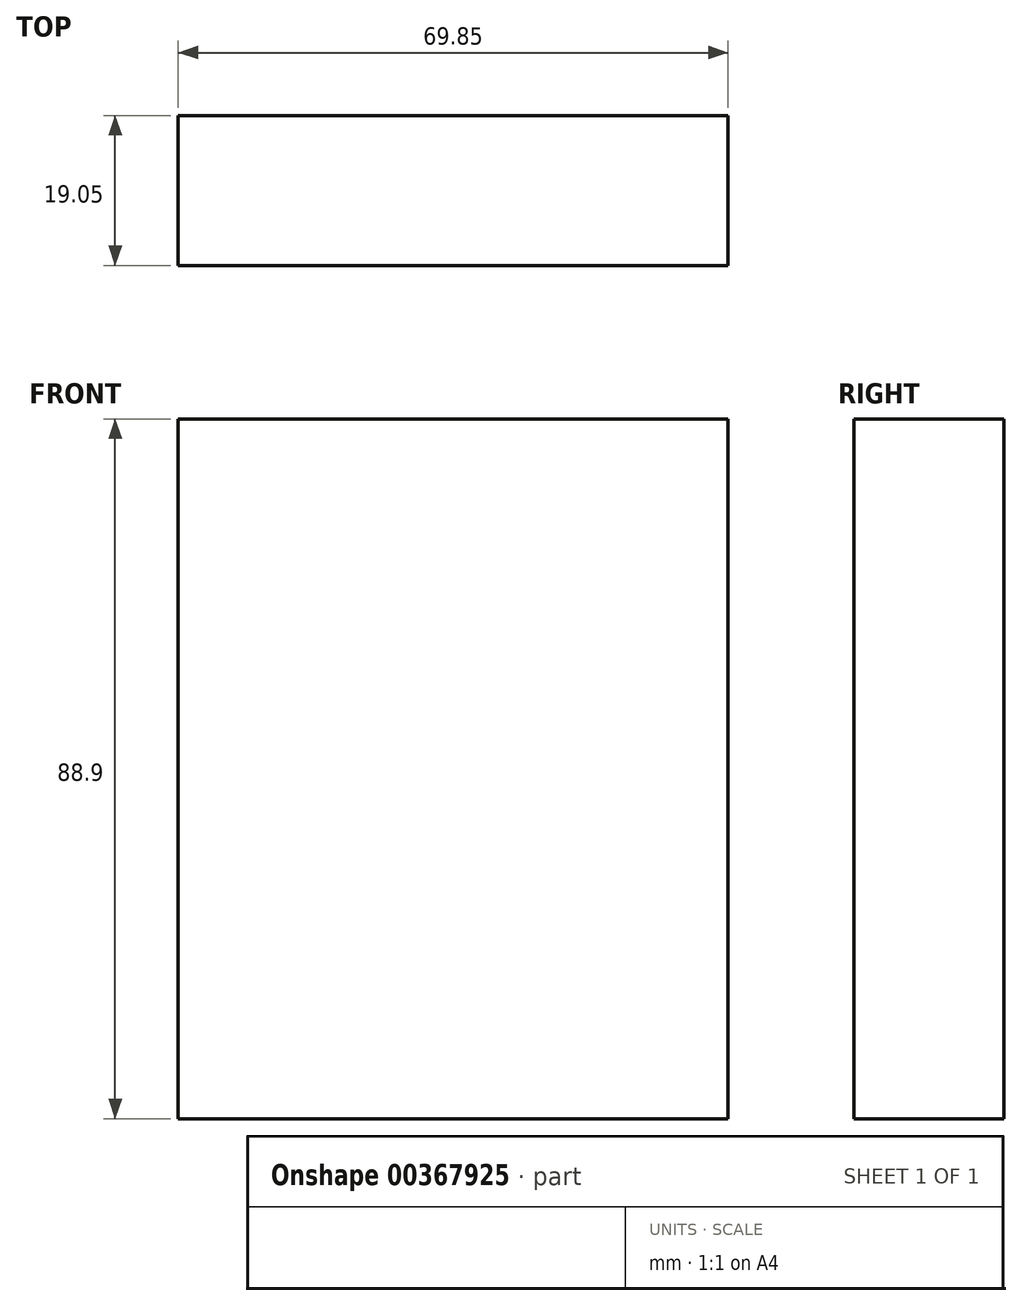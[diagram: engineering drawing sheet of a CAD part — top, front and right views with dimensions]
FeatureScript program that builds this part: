
annotation { "Feature Type Name" : "Feature", "Feature Type Description" : "" }
export const myFeature = defineFeature(function(context is Context, id is Id, definition is map)
    precondition{}
    {
        {
            var Q0;
            Q0=qCreatedBy(makeId("Front.planeOp"),FACE);
            var sketch = newSketch(context, id + "F0", { "sketchPlane" : qUnion([Q0])});
            skLineSegment(sketch, "E0.bottom", {"start": v(-88.51, 77.44) * mm, "end": v(-18.66, 77.44) * mm});
            skLineSegment(sketch, "E0.top", {"start": v(-88.51, -11.46) * mm, "end": v(-18.66, -11.46) * mm});
            skLineSegment(sketch, "E0.left", {"start": v(-88.51, 77.44) * mm, "end": v(-88.51, -11.46) * mm});
            skLineSegment(sketch, "E0.right", {"start": v(-18.66, 77.44) * mm, "end": v(-18.66, -11.46) * mm});
            skSolve(sketch);
        }
        {
            var Q0;
            Q0=makeQuery(id+"F0.imprint","IMPRINT",FACE,{"disambiguationData":[TD([[makeQuery(id+"F0.imprint","IMPRINT",EDGE,{"derivedFrom":sQuery(id+"F0.wireOp",EDGE,"E0.bottom")}),-1.0]])]});
            extrude(context, id + "F1", {"entities" : qUnion([Q0]), "depth" : 19.05 * mm});
        }
    });
